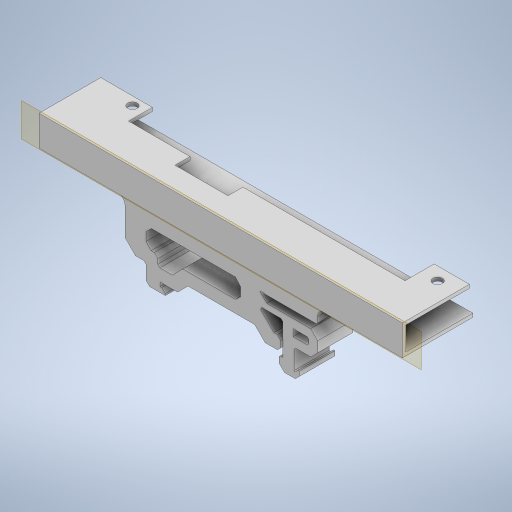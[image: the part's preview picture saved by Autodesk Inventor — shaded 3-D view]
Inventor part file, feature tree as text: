
AUTODESK INVENTOR PART (.ipt)
format: ipt  version: 2024 (Build 280153000, 153)  size: 471,552 bytes
history: native  units: in
note: dims shown in document units (in); Inventor stores cm internally (conversion verified against a paired STEP export)
features: extrude x5, sketch x2, fillet x2, plane x1
ambient origin geometry x8: Origin, YZ Plane, XZ Plane, XY Plane, X Axis, Y Axis, Z Axis, Center Point
bodies: Solid1 (feature_tree)
feature tree (10):
  sketch  "Sketch1"  dims[d0=0.1043in d1=0.1043in]
  extrude  "Extrusion1"  Depth=0.1043in
  extrude  "Extrusion2"  Depth=0.5768in
  extrude  "Extrusion3"  Depth=0.3937in
  extrude  "Extrusion4"  Depth=0.7087in
  plane  "Work Plane1"
  extrude  "Extrusion5"  Depth=0.6496in
  fillet  "Fillet1"  Radius=0.5541in
  fillet  "Fillet2"  Radius=0.4498in
  sketch  "Sketch5"  dims[d2=4.0591in d3=0.5768in d4=0.3937in d5=0.7087in d6=0.6496in d7=0.5541in d8=0.4498in d9=0.3839in d10=0.564in d11=0.2096in d12=0.0394in d13=0.0in d14=0.0394in d15=0.2992in d16=0.0in d17=0.0394in d18=0.748in d19=0.0in d21=0.5906in d23=0.0787in d24=0.0in d26=0.2559in d28=1.811in d29=0.2362in d30=0.3758in d31=0.1566in d32=0.1762in d33=0.1957in d34=0.1387in d35=0.1174in d36=0.0391in d37=0.0157in d38=2.1217in d39=0.0973in d40=0.0587in d41=0.0587in d42=0.0548in d43=0.0235in d44=0.9395in d45=0.0587in d46=0.0973in d47=0.5854in d48=0.1174in d49=0.7438in d50=0.1174in d51=0.1174in d52=0.137in d53=0.1475in d54=0.0277in d55=0.2143in d56=0.3464in d57=0.0196in d58=0.0626in d59=0.0137in d60=0.0274in d61=0.0607in d62=0.1213in d63=0.047in d64=0.0509in d65=0.0157in d66=0.0356in d67=0.0094in d68=0.2063in d69=0.0196in d70=0.1664in d71=0.0783in d72=0.1174in d73=0.0783in d74=0.4893in d75=0.0783in d76=0.6302in d77=0.0156in d78=0.1253in d79=0.1174in d80=0.1174in d81=0.1174in d82=0.0391in d83=0.0391in d84=0.0391in d85=0.1475in d86=0.0695in d87=0.0391in d88=0.0391in d89=0.0196in d90=0.0196in d91=0.0196in d92=0.0196in d93=0.0196in d94=0.0658in d95=0.0235in d96=0.0587in d97=0.0391in d98=0.0391in d99=0.0391in d100=0.0626in d101=0.0548in d102=0.0156in d103=0.0471in d104=0.0607in d105=0.0137in d106=0.0196in d107=0.094in d108=0.0196in d109=0.0156in d110=0.1376in d111=0.0352in d112=0.2349in d113=0.1566in d114=0.3568in d115=0.1566in d116=0.0115in d117=0.0156in d118=0.0772in d119=0.1751in d120=0.0984in d121=0.118in d122=4.0591in d123=2.153in d124=0.953in d125=0.3937in d126=0.0in d127=0.0787in d128=0.0787in]
